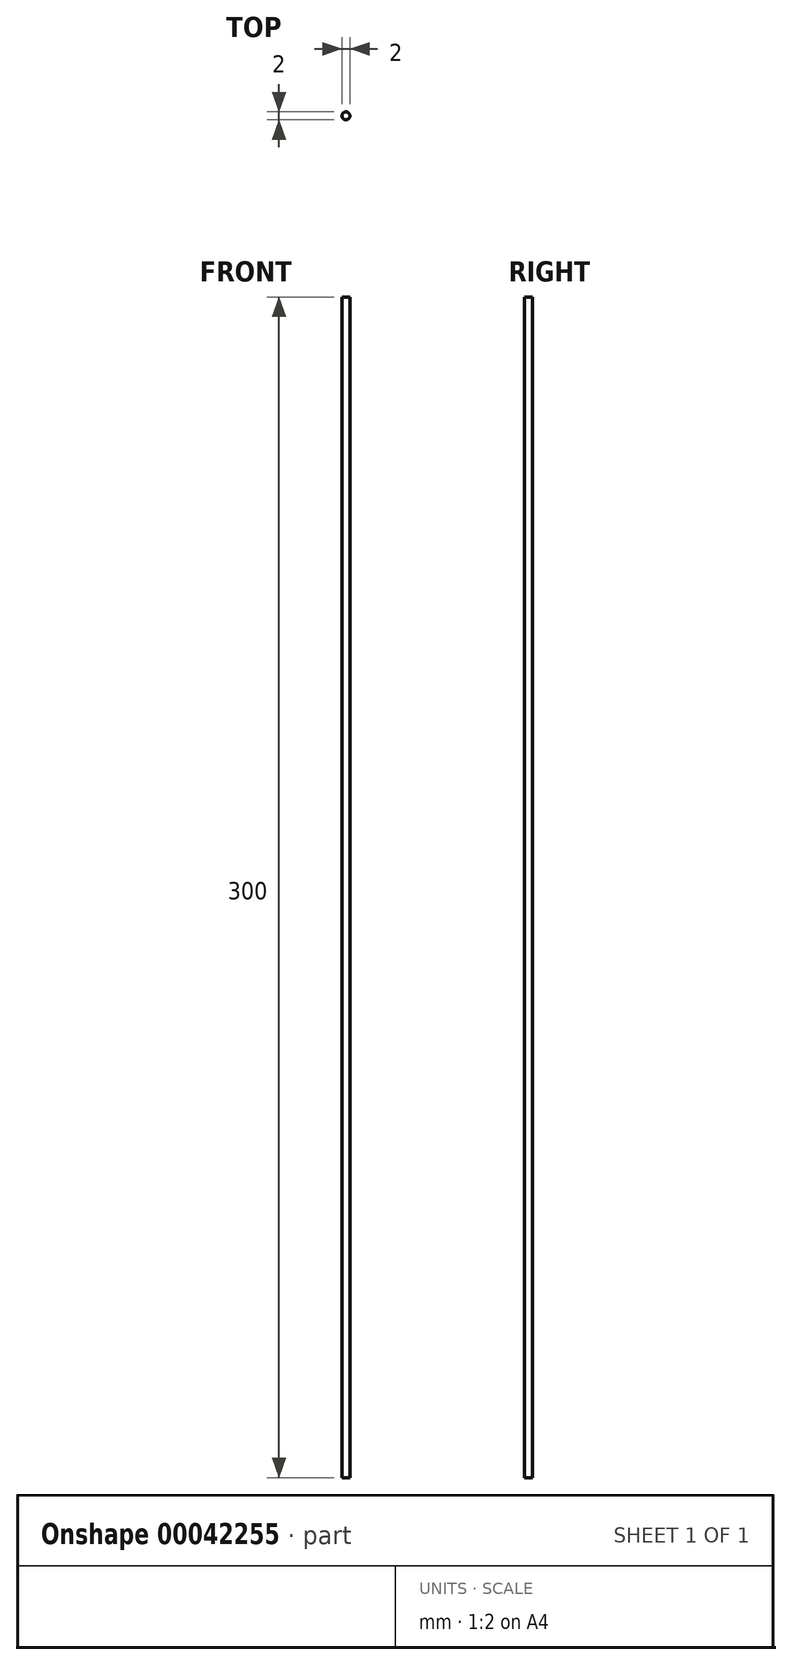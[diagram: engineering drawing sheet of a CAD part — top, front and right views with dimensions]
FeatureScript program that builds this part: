
annotation { "Feature Type Name" : "Feature", "Feature Type Description" : "" }
export const myFeature = defineFeature(function(context is Context, id is Id, definition is map)
    precondition{}
    {
        {
            var Q0;
            Q0=qCreatedBy(makeId("Top.planeOp"),FACE);
            var sketch = newSketch(context, id + "F0", { "sketchPlane" : qUnion([Q0])});
            skCircle(sketch, "E0", {"center": v(0, 0) * mm, "radius": 1 * mm});
            skSolve(sketch);
        }
        {
            var Q0;
            Q0 = qSketchRegion(id + "F0", true);
            extrude(context, id + "F1", {"entities" : qUnion([Q0]), "depth" : 300 * mm});
        }
    });
